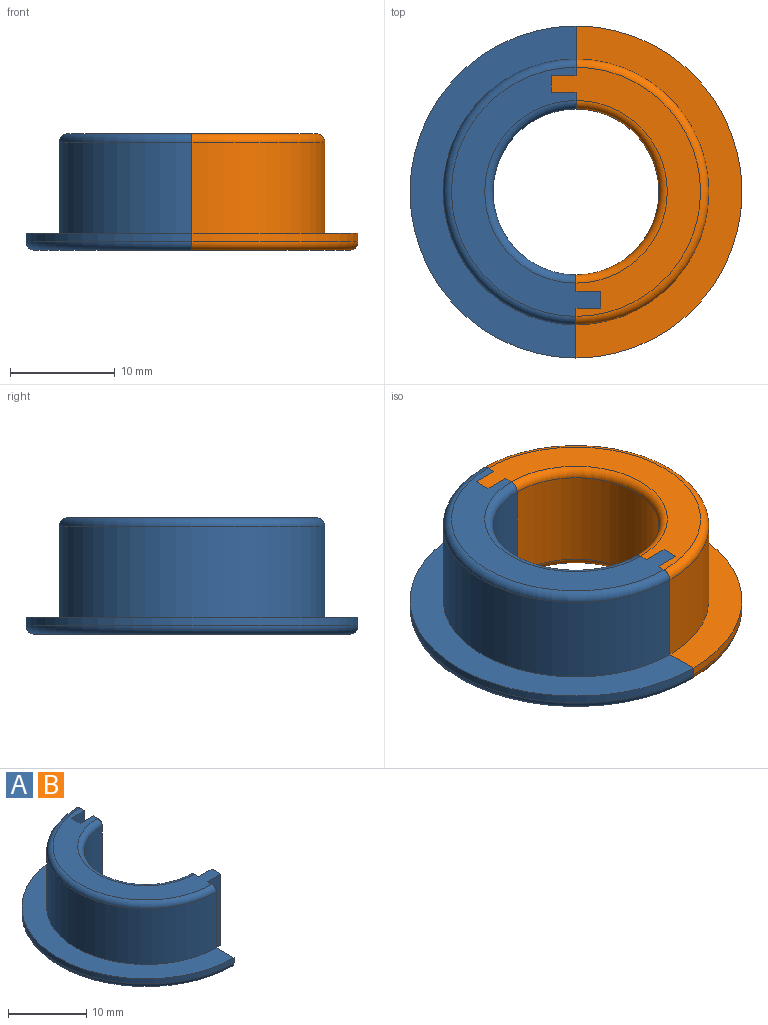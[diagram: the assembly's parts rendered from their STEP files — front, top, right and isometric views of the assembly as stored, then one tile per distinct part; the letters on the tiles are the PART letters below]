
ASSEMBLY  parts=2 mates=1
PART A: 20 faces, bbox 19.6x34.4x11.1 mm
  f0: cylinder r=15.88mm len=31.75mm, axis (0,0,1), area 39.6mm2, adj f2,f3,f4,f14
  f1: plane 30.16x17.46mm, normal (0,0,-1), area 237.5mm2, adj f3,f4,f5,f6,f7,f8,f10,f11
  f2: plane 31.75x15.88mm, normal (0,0,1), area 142.5mm2, adj f0,f4,f14,f15
  f3: torus R=15.08mm, axis (0,0,1), area 61.1mm2, adj f0,f1,f4,f14
  f4: plane 11.11x4.76mm, normal (1,0,0), area 22.4mm2, adj f0,f1,f2,f3,f5,f15,f16,f19
  f5: plane 11.11x2.38mm, normal (0,-1,0), area 26.5mm2, adj f1,f4,f6,f16
  f6: plane 11.11x1.59mm, normal (1,0,0), area 17.6mm2, adj f1,f5,f7,f16
  f7: plane 11.11x2.38mm, normal (0,1,0), area 26.5mm2, adj f1,f6,f8,f16
  f8: plane 11.11x1.59mm, normal (1,0,0), area 17.4mm2, adj f1,f7,f9,f16,f17,f18
  f9: cylinder r=7.94mm len=15.88mm, axis (0,0,-1), area 237.5mm2, adj f8,f10,f17,f18
  f10: plane 11.11x1.59mm, normal (1,0,0), area 17.4mm2, adj f1,f9,f11,f16,f17,f18
  f11: plane 11.11x2.38mm, normal (0,1,0), area 26.5mm2, adj f1,f10,f12,f16
  f12: plane 11.11x1.59mm, normal (1,0,0), area 17.6mm2, adj f1,f11,f13,f16
  f13: plane 11.11x2.38mm, normal (0,-1,0), area 26.5mm2, adj f1,f12,f14,f16
  f14: plane 11.11x4.76mm, normal (1,0,0), area 22.4mm2, adj f0,f1,f2,f3,f13,f15,f16,f19
  f15: cylinder r=12.7mm len=25.4mm, axis (0,0,-1), area 348.4mm2, adj f2,f4,f14,f19
  f16: plane 23.81x14.29mm, normal (0,0,1), area 102.9mm2, adj f4,f5,f6,f7,f8,f10,f11,f12
  f17: torus R=8.73mm, axis (0,0,1), area 32.2mm2, adj f1,f8,f9,f10
  f18: torus R=8.73mm, axis (0,0,1), area 32.2mm2, adj f8,f9,f10,f16
  f19: torus R=11.91mm, axis (0,0,1), area 48.6mm2, adj f4,f14,f15,f16
PART B: same geometry as A
PLACE A rot(axis=(0,0,-1),0deg) t=(-4.21,4.13,-3.64)mm
PLACE B rot(axis=(0,0,1),180deg) t=(-4.21,4.13,-3.64)mm
MATE slider A.f16 <-> B.f16  axis (0,0,1) through (-1.83,-5.4,5.89)mm
